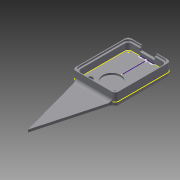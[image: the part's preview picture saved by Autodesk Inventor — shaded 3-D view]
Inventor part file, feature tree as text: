
AUTODESK INVENTOR PART (.ipt)
format: ipt  version: 2015 SP1 (Build 190203100, 203)  size: 185,856 bytes
history: native  units: mm
features: sketch x7, extrude x5, fillet x4, other x2, projected_geometry x1, reference x1
ambient origin geometry x8: Origin, YZ Plane, XZ Plane, XY Plane, X Axis, Y Axis, Z Axis, Center Point
bodies: Body1 (feature_tree)
feature tree (20):
  other  "Sólido1"
  extrude  "Extrusión1"  Depth=34.0mm
  sketch  "Boceto2"  dims[d2=5.5mm d3=5.5mm d4=3.0mm]
  extrude  "Extrusión2"  Depth=5.5mm
  fillet  "Empalme1"  Radius=3.0mm
  sketch  "Boceto4"  dims[d12=9.0mm d15=40.0mm]
  extrude  "Extrusión4"  Depth=23.0mm
  fillet  "Empalme2"  Radius=31.0mm
  fillet  "Empalme3"  Radius=5.0mm
  fillet  "Empalme4"  Radius=2.0mm
  other  "Labio1"
  extrude  "Extrusión5"  Depth=9.0mm
  extrude  "Extrusión6"  Depth=2.0mm
  sketch  "Boceto1"  dims[d0=26.0mm d1=34.0mm]
  sketch  "Boceto3"  dims[d5=2.0mm d6=0.0mm d7=23.0mm d8=31.0mm d9=5.0mm d10=0.0mm d11=2.0mm]
  sketch  "Boceto5"  dims[d16=1.5mm d17=0.0mm d18=2.0mm]
  projected_geometry  "Contorno proyectado1"
  sketch  "Boceto7"  dims[d19=2.0mm]
  sketch  "Boceto8"  dims[d20=2.0mm d21=1.0mm d22=1.0mm d23=0.0mm d24=0.0mm d25=0.0mm d26=0.0mm d27=2.0mm d28=4.0mm d29=0.0mm d30=0.0mm d31=1.0mm d32=0.0mm]
  reference  "Referencia2"
